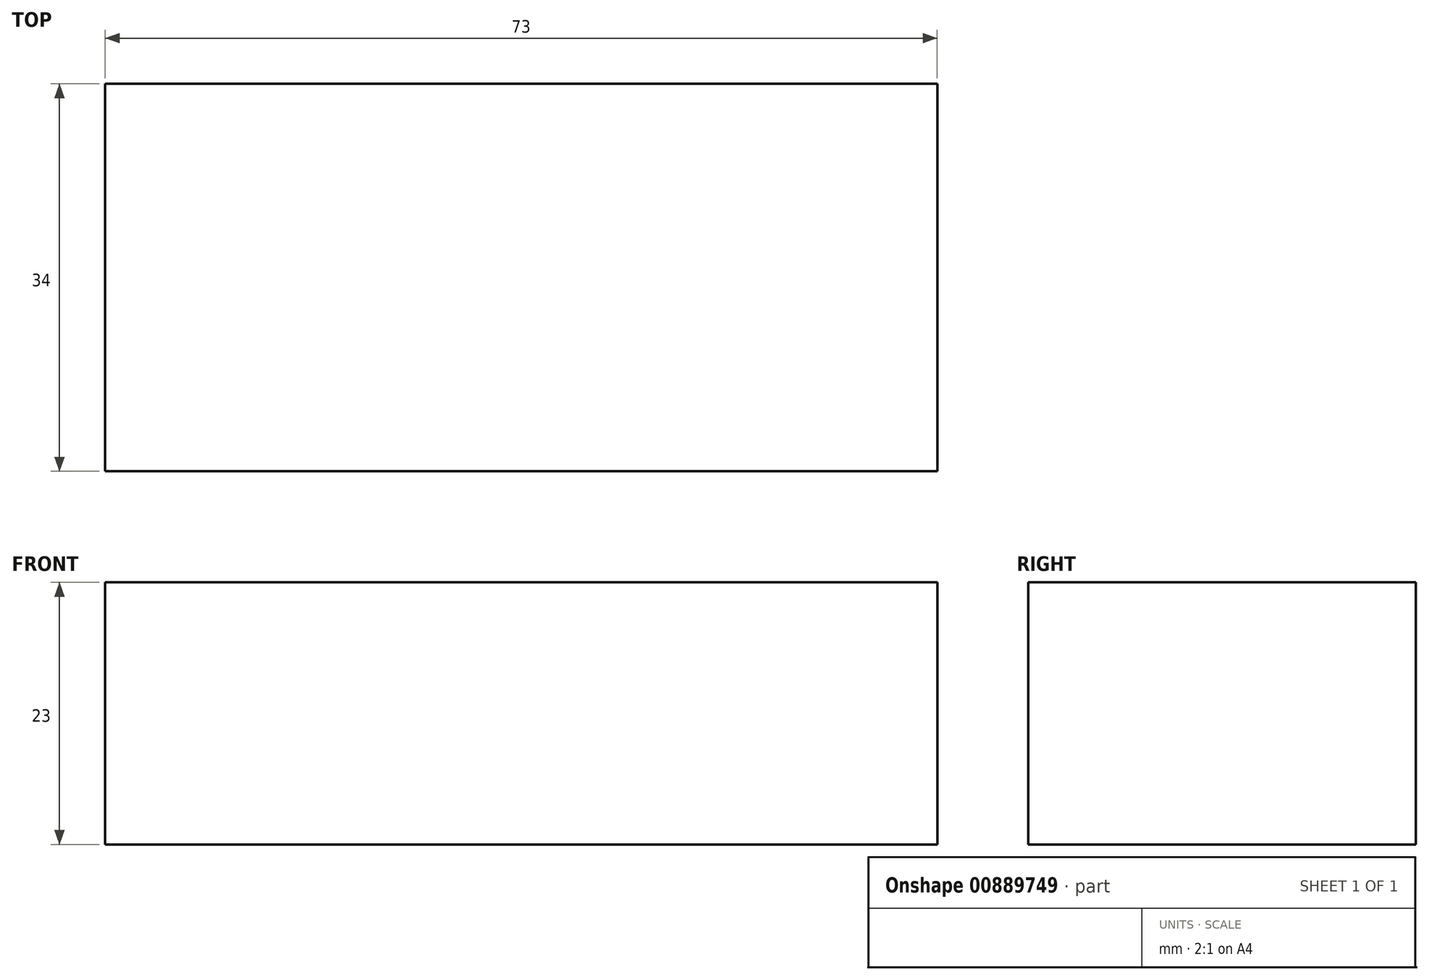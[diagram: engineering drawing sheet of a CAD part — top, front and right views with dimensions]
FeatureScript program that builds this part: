
annotation { "Feature Type Name" : "Feature", "Feature Type Description" : "" }
export const myFeature = defineFeature(function(context is Context, id is Id, definition is map)
    precondition{}
    {
        {
            var Q0;
            Q0=qCreatedBy(makeId("Top.planeOp"),FACE);
            var sketch = newSketch(context, id + "F0", { "sketchPlane" : qUnion([Q0])});
            skLineSegment(sketch, "E0.bottom", {"start": v(-35.99, 12.19) * mm, "end": v(37.01, 12.19) * mm});
            skLineSegment(sketch, "E0.top", {"start": v(-35.99, -21.81) * mm, "end": v(37.01, -21.81) * mm});
            skLineSegment(sketch, "E0.left", {"start": v(-35.99, 12.19) * mm, "end": v(-35.99, -21.81) * mm});
            skLineSegment(sketch, "E0.right", {"start": v(37.01, 12.19) * mm, "end": v(37.01, -21.81) * mm});
            skSolve(sketch);
        }
        {
            var Q0;
            Q0=qSketchRegion(id+"F0",true);
            extrude(context, id + "F1", {"entities" : qUnion([Q0]), "depth" : 23 * mm});
        }
    });
